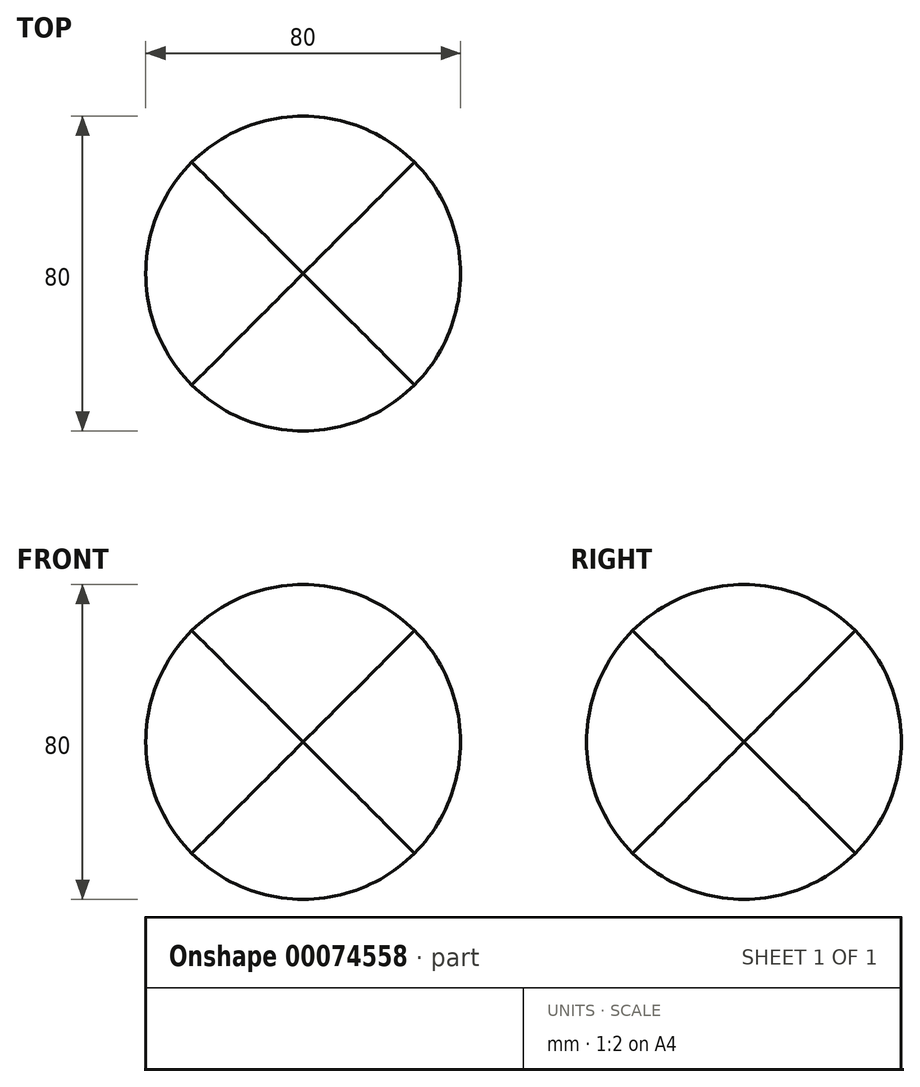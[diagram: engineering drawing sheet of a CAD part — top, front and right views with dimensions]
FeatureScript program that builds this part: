
annotation { "Feature Type Name" : "Feature", "Feature Type Description" : "" }
export const myFeature = defineFeature(function(context is Context, id is Id, definition is map)
    precondition{}
    {
        {
            var Q0;
            Q0=qCreatedBy(makeId("Front.planeOp"),FACE);
            var sketch = newSketch(context, id + "F0", { "sketchPlane" : qUnion([Q0])});
            skCircle(sketch, "E0", {"center": v(0, 0) * mm, "radius": 40 * mm});
            skSolve(sketch);
        }
        {
            var Q0;
            Q0=makeQuery(id+"F0.imprint","IMPRINT",FACE,{"disambiguationData":[TD([[makeQuery(id+"F0.imprint","IMPRINT",EDGE,{"derivedFrom":sQuery(id+"F0.wireOp",EDGE,"E0")}),1.0]])]});
            var Q1;
            Q1=sQuery(id+"F0.wireOp",EDGE,"E0");
            extrude(context, id + "F1", {"entities" : qUnion([Q0]), "surfaceEntities" : qUnion([Q1]), "depth" : 200 * mm, "symmetric" : true});
        }
        {
            var Q0;
            Q0=qCreatedBy(makeId("Top.planeOp"),FACE);
            var sketch = newSketch(context, id + "F2", { "sketchPlane" : qUnion([Q0])});
            skCircle(sketch, "E1", {"center": v(0, 0) * mm, "radius": 40 * mm});
            skSolve(sketch);
        }
        {
            var Q0;
            Q0 = qSketchRegion(id + "F2", true);
            extrude(context, id + "F3", {"entities" : qUnion([Q0]), "operationType" : NewBodyOperationType.INTERSECT, "oppositeDirection" : true, "depth" : 200 * mm, "symmetric" : true});
        }
        {
            var Q0;
            Q0=qCreatedBy(makeId("Right.planeOp"),FACE);
            var sketch = newSketch(context, id + "F4", { "sketchPlane" : qUnion([Q0])});
            skCircle(sketch, "E2", {"center": v(0, 0) * mm, "radius": 40 * mm});
            skSolve(sketch);
        }
        {
            var Q0;
            Q0 = qSketchRegion(id + "F4", true);
            extrude(context, id + "F5", {"entities" : qUnion([Q0]), "operationType" : NewBodyOperationType.INTERSECT, "oppositeDirection" : true, "depth" : 200 * mm, "symmetric" : true});
        }
    });
